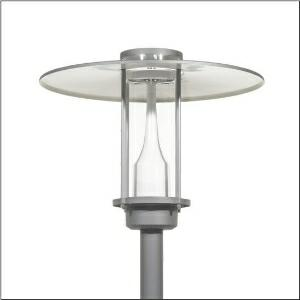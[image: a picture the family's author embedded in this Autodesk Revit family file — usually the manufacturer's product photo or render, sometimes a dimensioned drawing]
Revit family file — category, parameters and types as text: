
# Revit family: city-light_plus_iq___st1_2a_5xa5275ef14h000022_292e
name_source: partatom
category: Lighting Fixtures
units: mm (PartAtom-declared; Revit-internal decimal feet)

## family parameters
Cut with Voids When Loaded = No
Host = Face
Light Source = No
Part Type = Normal
Room Calculation Point = No
Round Connector Dimension = Use Diameter
Shared = No

## types (1)
- --- (1 x LED, 1470 lm, 10.5 W, 3000K)
    Apparent Load = 11 VA
    CIE Flux Codes = 22 62 93 97 100
    Color Rendering = 70
    Color Temperature = 3000K
    Default Elevation = 1800 mm
    Description = City-Light Plus iQ, mast luminaire, Module 540 iQ-SR, primary light control with 3 zone facetted reflector, of plastic, silver coated, highly specular, structured, primary optical cover: cover, of PMMA, transparent, light distribution: ST1.2a, light emission: direct distribution, primary light characteristic: asymmetric, installation type: post-top, LED, High Power LED, rated luminous flux: 1.470lm, luminous efficacy: 140lm/W, light colour: 730, colour temperature: 3000K, control gear: iQ Street-Remote, control: Street-Remote, Auto-Match, Temp-Guard, Lumen-Switch, Night-Set, Smart-Wire, Light-Fading, Desk-Remote (wireless, voltage-free reading and setting of iQ features in the workshop via application-optimized NFC function/RFID function), optimised constant luminous flux control (CLO 2.0), pre-setting: logarithmic dimming characteristic, mains connection: 230..240V, AC, 50/60Hz, connection cable pre-assembled, cable length: 5,5m, wiring characteristics: H07RN-F, start of lifetime: 11W, end of service life: 11W, reduction: 5W, luminaire housing, upper part, of glass-fibre reinforced polyester, coated, Siteco® metallic grey (DB 702S), diameter: 750mm, height: 590mm, spigot size: d x l = 76 x 70mm (post-top) | with reducer (optional accessory) 60 x 70mm, mounting height: 3..5m, post-top mast mounting element, of diecast aluminium, coated, Siteco® metallic grey (DB 702S), Module 540 iQ-SR, traffic white (RAL 9016), equipment: standard, protection rating (complete): IP65, insulation class (complete): insulation class II (safety insulation), certification: CE, ENEC, VDE, packaging unit: 1 piece

Light Distribution: ST1.2a
    Height = 590 mm
    Lamp = 1 x LED
    Lamp Light Flux = 1470 lm
    Lamp Power = 10.5 W
    Lamp count = 1
    Length = 750 mm
    Luminous efficacy = 140 lm/W
    Manufacturer = Siteco
    ModVariant = No
    Model = 5XA5275EF14H000022
    Number of Poles = 1
    OnlyDefault = Yes
    Power Factor = 1
    Product Name = City-Light Plus iQ | ST1.2a
    Product group = mast luminaire | pylon top
    ProductGroupID = 6100
    Protection Class = Protection class II
    Protection Degree = IP 65
    RLX_Detail_Level = 1
    RLX_Emergency_Light_Flux = 0 lm
    RLX_Emergency_Type = 0
    RLX_Emergency_Type_DB = No
    RlxData = <blob elided: 34049 chars, md5=c0541153>
    Socket = socket
    Standby Power = 0 W
    System Light Flux = 1470 lm
    System Power = 11 W
    Type Comments = factory setting: luminous flux: 100 % | dim-lin: 254 | 419 mA
    Type Image = l_1006456.jpg
    URL = http://relux.com
    VarID = @adj_181517
    Voltage = 0 V
    Weight = 0.00 kg
    Width = 0 mm  [stored 0 ft]

note: [stored X ft] marks values corroborated as IEEE doubles in the binary element streams (Revit-internal decimal feet)

## geometry (parser evidence)
native form markers: Blend x4, Sweep x11
no freeform markers — native parametric forms only
